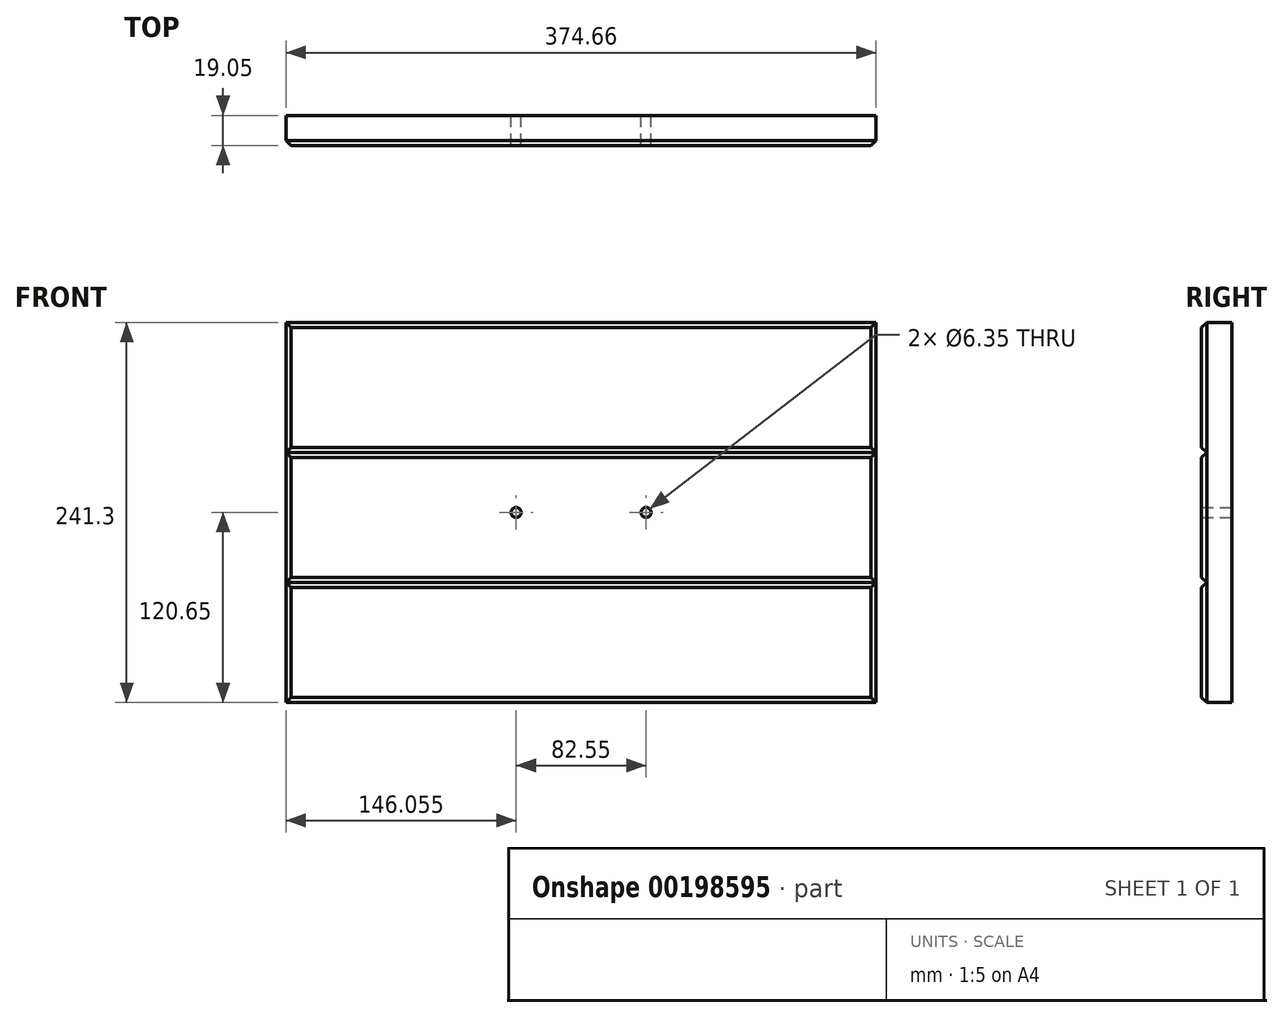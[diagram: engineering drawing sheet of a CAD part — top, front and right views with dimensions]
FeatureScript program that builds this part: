
annotation { "Feature Type Name" : "Feature", "Feature Type Description" : "" }
export const myFeature = defineFeature(function(context is Context, id is Id, definition is map)
    precondition{}
    {
        {
            var Q0;
            Q0=qCreatedBy(makeId("Front.planeOp"),FACE);
            var sketch = newSketch(context, id + "F0", { "sketchPlane" : qUnion([Q0])});
            skLineSegment(sketch, "E0.bottom", {"start": v(187.33, 120.65) * mm, "end": v(-187.33, 120.65) * mm});
            skLineSegment(sketch, "E0.top", {"start": v(187.33, -120.65) * mm, "end": v(-187.33, -120.65) * mm});
            skLineSegment(sketch, "E0.left", {"start": v(187.33, 120.65) * mm, "end": v(187.33, -120.65) * mm});
            skLineSegment(sketch, "E0.right", {"start": v(-187.33, 120.65) * mm, "end": v(-187.33, -120.65) * mm});
            skPoint(sketch, "E0.middle", {"position": v(0, 0) * mm});
            skSolve(sketch);
        }
        {
            var Q0;
            Q0 = qSketchRegion(id + "F0", true);
            extrude(context, id + "F1", {"entities" : qUnion([Q0]), "depth" : 19.05 * mm});
        }
        {
            var Q0;
            Q0=makeQuery(id+"F1.opExtrude","SWEPT_FACE",FACE,{"disambiguationData":[OSD([sQuery(id+"F0.wireOp",EDGE,"E0.right")])]});
            var sketch = newSketch(context, id + "F2", { "sketchPlane" : qUnion([Q0])});
            skLineSegment(sketch, "E1", {"start": v(19.05, 38.1) * mm, "end": v(19.05, 34.92) * mm});
            skLineSegment(sketch, "E2", {"start": v(15.88, 38.1) * mm, "end": v(19.05, 41.27) * mm});
            skLineSegment(sketch, "E3", {"start": v(15.88, 38.1) * mm, "end": v(19.05, 34.92) * mm});
            skLineSegment(sketch, "E4", {"start": v(15.88, -44.45) * mm, "end": v(19.05, -41.28) * mm});
            skLineSegment(sketch, "E5", {"start": v(15.88, -44.45) * mm, "end": v(19.05, -47.63) * mm});
            skLineSegment(sketch, "E6", {"start": v(19.05, -41.28) * mm, "end": v(19.05, -47.63) * mm});
            skLineSegment(sketch, "E7", {"start": v(19.05, 41.27) * mm, "end": v(19.05, 34.92) * mm});
            skSolve(sketch);
        }
        {
            var Q0;
            Q0 = qSketchRegion(id + "F2", true);
            extrude(context, id + "F3", {"entities" : qUnion([Q0]), "operationType" : NewBodyOperationType.REMOVE, "endBound" : BoundingType.THROUGH_ALL, "oppositeDirection" : true, "depth" : 25.4 * mm});
        }
        {
            var Q0;
            Q0=makeQuery(id+"F1.opExtrude","CAP_EDGE",EDGE,{"disambiguationData":[OSD([sQuery(id+"F0.wireOp",EDGE,"E0.bottom")])],"isStart":false});
            var Q1;
            Q1=makeQuery(id+"F1.opExtrude","CAP_EDGE",EDGE,{"disambiguationData":[OSD([sQuery(id+"F0.wireOp",EDGE,"E0.top")])],"isStart":false});
            var Q2;
            {var subQ0=sQuery(id+"F0.wireOp",EDGE,"E0.left");Q2=makeQuery(id+"F3.boolean.opBoolean","SPLIT",EDGE,{"disambiguationData":[TD([makeQuery(id+"F3.opExtrude","SWEPT_FACE",FACE,{"disambiguationData":[OSD([sQuery(id+"F2.wireOp",EDGE,"E3")])]})])],"derivedFrom":makeQuery(id+"F1.opExtrude","CAP_EDGE",EDGE,{"disambiguationData":[OSD([subQ0])],"isStart":false})});}
            var Q3;
            {var subQ0=sQuery(id+"F0.wireOp",EDGE,"E0.left");var subQ1=sQuery(id+"F0.wireOp",EDGE,"E0.top");Q3=makeQuery(id+"F3.boolean.opBoolean","SPLIT",EDGE,{"disambiguationData":[TD([makeQuery(id+"F1.opExtrude","SWEPT_FACE",FACE,{"disambiguationData":[OSD([subQ1])]})])],"derivedFrom":makeQuery(id+"F1.opExtrude","CAP_EDGE",EDGE,{"disambiguationData":[OSD([subQ0])],"isStart":false})});}
            var Q4;
            {var subQ0=sQuery(id+"F0.wireOp",EDGE,"E0.bottom");var subQ1=sQuery(id+"F0.wireOp",EDGE,"E0.left");Q4=makeQuery(id+"F3.boolean.opBoolean","SPLIT",EDGE,{"disambiguationData":[TD([makeQuery(id+"F1.opExtrude","SWEPT_FACE",FACE,{"disambiguationData":[OSD([subQ0])]})])],"derivedFrom":makeQuery(id+"F1.opExtrude","CAP_EDGE",EDGE,{"disambiguationData":[OSD([subQ1])],"isStart":false})});}
            var Q5;
            {var subQ0=sQuery(id+"F0.wireOp",EDGE,"E0.right");Q5=makeQuery(id+"F3.boolean.opBoolean","SPLIT",EDGE,{"disambiguationData":[TD([makeQuery(id+"F3.opExtrude","SWEPT_FACE",FACE,{"disambiguationData":[OSD([sQuery(id+"F2.wireOp",EDGE,"E3")])]})])],"derivedFrom":makeQuery(id+"F1.opExtrude","CAP_EDGE",EDGE,{"disambiguationData":[OSD([subQ0])],"isStart":false})});}
            var Q6;
            {var subQ0=sQuery(id+"F0.wireOp",EDGE,"E0.right");var subQ1=sQuery(id+"F0.wireOp",EDGE,"E0.top");Q6=makeQuery(id+"F3.boolean.opBoolean","SPLIT",EDGE,{"disambiguationData":[TD([makeQuery(id+"F1.opExtrude","SWEPT_FACE",FACE,{"disambiguationData":[OSD([subQ1])]})])],"derivedFrom":makeQuery(id+"F1.opExtrude","CAP_EDGE",EDGE,{"disambiguationData":[OSD([subQ0])],"isStart":false})});}
            var Q7;
            {var subQ0=sQuery(id+"F0.wireOp",EDGE,"E0.bottom");var subQ1=sQuery(id+"F0.wireOp",EDGE,"E0.right");Q7=makeQuery(id+"F3.boolean.opBoolean","SPLIT",EDGE,{"disambiguationData":[TD([makeQuery(id+"F1.opExtrude","SWEPT_FACE",FACE,{"disambiguationData":[OSD([subQ0])]})])],"derivedFrom":makeQuery(id+"F1.opExtrude","CAP_EDGE",EDGE,{"disambiguationData":[OSD([subQ1])],"isStart":false})});}
            chamfer(context, id + "F4", {"entities" : qUnion([Q0, Q1, Q2, Q3, Q4, Q5, Q6, Q7]), "width" : 3.17 * mm, "tangentPropagation" : true});
        }
        {
            var Q0;
            Q0=makeQuery(id+"F1.opExtrude","CAP_FACE",FACE,{"disambiguationData":[OSD([sQuery(id+"F0.wireOp",EDGE,"E0.bottom"),sQuery(id+"F0.wireOp",EDGE,"E0.top"),sQuery(id+"F0.wireOp",EDGE,"E0.left"),sQuery(id+"F0.wireOp",EDGE,"E0.right")])],"isStart":true});
            var sketch = newSketch(context, id + "F5", { "sketchPlane" : qUnion([Q0])});
            skPoint(sketch, "E8.endSnap0", {"position": v(0, 120.65) * mm});
            skCircle(sketch, "E9", {"center": v(41.28, 0) * mm, "radius": 3.18 * mm});
            skCircle(sketch, "E10", {"center": v(-41.28, 0) * mm, "radius": 3.18 * mm});
            skSolve(sketch);
        }
        {
            var Q0;
            Q0 = qSketchRegion(id + "F5", true);
            extrude(context, id + "F6", {"entities" : qUnion([Q0]), "operationType" : NewBodyOperationType.REMOVE, "oppositeDirection" : true, "depth" : 25.4 * mm});
        }
    });
